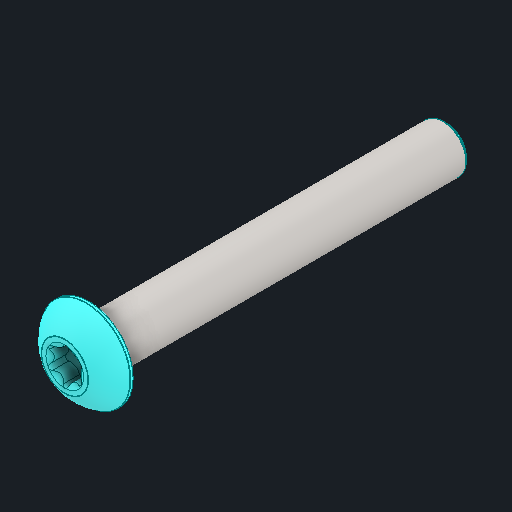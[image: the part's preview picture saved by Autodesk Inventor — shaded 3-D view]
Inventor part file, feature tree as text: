
AUTODESK INVENTOR PART (.ipt)
format: ipt  version: 2025 (Build 290162000, 162)  size: 157,696 bytes
history: native  units: in
note: dims shown in document units (in); Inventor stores cm internally (conversion verified against a paired STEP export)
features: fillet x1
ambient origin geometry x8: Origin, YZ Plane, XZ Plane, XY Plane, X Axis, Y Axis, Z Axis, Center Point
bodies: Solid1 (feature_tree)
feature tree (1):
  fillet  "Fillet1"  [1 undecoded]
note: 1 required parameter value undecoded (feature->parameter linkage not recoverable at this tier; creation-order binding heuristic only, values carry confidence <= 0.55)
